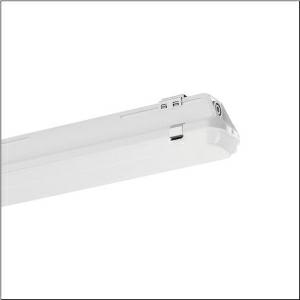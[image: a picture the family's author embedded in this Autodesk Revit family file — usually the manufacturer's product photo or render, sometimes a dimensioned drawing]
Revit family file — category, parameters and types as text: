
# Revit family: monsun_21_51fb107p430k
name_source: partatom
category: Lighting Fixtures
units: mm (PartAtom-declared; Revit-internal decimal feet)

## family parameters
Cut with Voids When Loaded = No
Host = Face
Light Source = No
Part Type = Normal
Room Calculation Point = No
Round Connector Dimension = Use Diameter
Shared = No

## types (1)
- Monsun 21 (1 x LED, 3940 lm, 22.1 W, 4000K)
    Apparent Load = 22 VA
    CIE Flux Codes = 47 77 93 94 100
    Color Rendering = 80
    Color Temperature = 4000K
    Default Elevation = 1800 mm
    Description = Monsun 21, damp-proof luminaire, chain hanger, primary optical cover: enclosure, of PMMA, light emission: direct distribution, primary light characteristic: symmetric, installation type: suspended mounting, surface-mounted, horizontal mounting, vertical mounting, LED, rated luminous flux: 3.940lm, luminous efficacy: 178lm/W, light colour: 840, colour temperature: 4000K, control gear: ON/OFF, with terminal, 3-pole, max. 2.5mm², mains connection: 220..240V, AC, 50/60Hz, rated input power: 22W, housing, of glass-fibre reinforced polyester, uncoated, bright grey, incl. chain hanger, length: 1.590mm, width: 90mm, height: 88mm, clip for enclosure, of stainless steel (V2A), ceiling mounting element, of stainless steel (V2A), chain hanger, of stainless steel (V2A), protection rating (complete): IP66, insulation class (complete): insulation class I (protective earthing), certification: CE, ENEC, VDE, UKCA, protection symbol: D, impact resistance: IK04, permissible operating ambient temperature: -25..+35°C, standard: EN 50419, EN 60598-2-1, corresponds to IFS (International Featured Standards) requirements for safety and quality in the food industry, for indoor or canopied outdoor use, no direct snow, no direct sun, no direct rain, LABS conformity tested according to VDMA 24364:2018-05, contact your sales advisor before using the luminaires in applications with unclear chemical exposure, large temperature fluctuations or condensation-forming humidity, packaging unit: 1 piece
    Height = 89 mm
    Lamp = 1 x LED
    Lamp Light Flux = 3940 lm
    Lamp Power = 22.1 W
    Lamp count = 1
    Length = 1590 mm
    Luminous efficacy = 178 lm/W
    Manufacturer = Siteco
    ModVariant = No
    Model = 51FB107P430K
    Mounting Place = Ceiling
    Mounting Type = Surface mounted
    Number of Poles = 1
    OnlyDefault = Yes
    Power Factor = 1
    Product Name = Monsun 21
    Product group = damp-proof luminaire
    ProductGroupID = 300
    Protection Class = Protection class I
    Protection Degree = IP 66
    RLX_Detail_Level = 1
    RLX_Emergency_Light_Flux = 0 lm
    RLX_Emergency_Type = 0
    RLX_Emergency_Type_DB = No
    RlxData = <blob elided: 88609 chars, md5=38516e29>
    Socket = socket
    Standby Power = 0 W
    System Light Flux = 3940 lm
    System Power = 22 W
    Type Comments = Product without accessories
    Type Image = l_1319656.jpg
    URL = http://relux.com
    VarID = ---
    Voltage = 0 V
    Weight = 0.00 kg
    Width = 90 mm

## geometry (parser evidence)
native form markers: Blend x4, Sweep x13
no freeform markers — native parametric forms only
